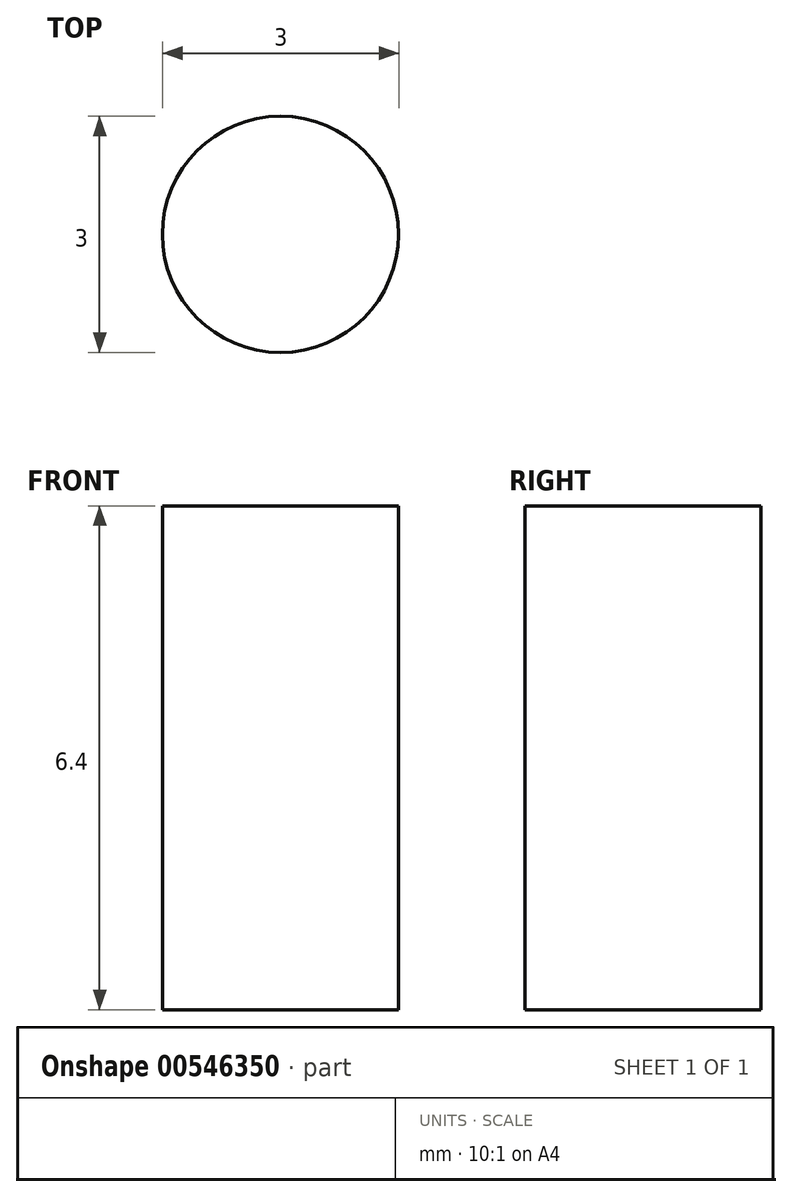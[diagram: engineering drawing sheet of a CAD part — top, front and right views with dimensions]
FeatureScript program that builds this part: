
annotation { "Feature Type Name" : "Feature", "Feature Type Description" : "" }
export const myFeature = defineFeature(function(context is Context, id is Id, definition is map)
    precondition{}
    {
        {
            var Q0;
            Q0=qCreatedBy(makeId("Top.planeOp"),FACE);
            var sketch = newSketch(context, id + "F0", { "sketchPlane" : qUnion([Q0])});
            skCircle(sketch, "E0", {"center": v(-19.8, 17.73) * mm, "radius": 1.5 * mm});
            skPoint(sketch, "E0.first.point", {"position": v(-21.3, 17.72) * mm});
            skPoint(sketch, "E0.second.point", {"position": v(-19.55, 16.25) * mm});
            skPoint(sketch, "E0.third.point", {"position": v(-20.33, 16.33) * mm});
            skSolve(sketch);
        }
        {
            var Q0;
            Q0 = qSketchRegion(id + "F0", true);
            extrude(context, id + "F1", {"entities" : qUnion([Q0]), "depth" : 6.4 * mm, "offsetDistance" : 25 * mm});
        }
    });
